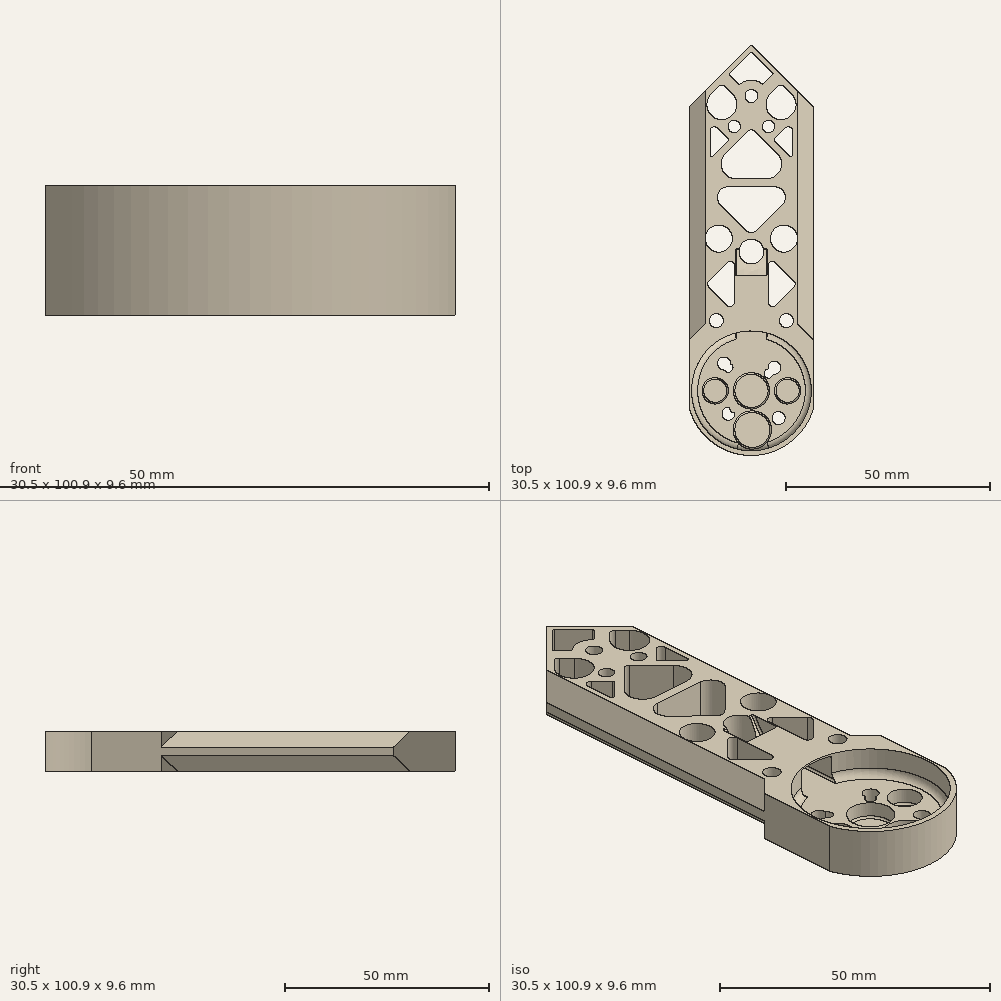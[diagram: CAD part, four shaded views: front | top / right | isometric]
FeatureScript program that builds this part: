
annotation { "Feature Type Name" : "Feature", "Feature Type Description" : "" }
export const myFeature = defineFeature(function(context is Context, id is Id, definition is map)
    precondition{}
    {
        {
            var Q0;
            Q0=qCreatedBy(makeId("Top.planeOp"),FACE);
            var sketch = newSketch(context, id + "F0", { "sketchPlane" : qUnion([Q0])});
            skLineSegment(sketch, "E0", {"start": v(0, 0) * mm, "end": v(-10, 0) * mm});
            skLineSegment(sketch, "E1", {"start": v(-7.84, 7.84) * mm, "end": v(0, 0) * mm});
            skLineSegment(sketch, "E2", {"start": v(-6.78, -6.78) * mm, "end": v(0, 0) * mm});
            skLineSegment(sketch, "E3", {"start": v(0, 0) * mm, "end": v(-5.66, -5.66) * mm});
            skCircle(sketch, "E4", {"center": v(-5.66, -5.66) * mm, "radius": 1.59 * mm});
            skLineSegment(sketch, "E5", {"start": v(0, 0) * mm, "end": v(-6.72, 6.72) * mm});
            skCircle(sketch, "E6", {"center": v(-6.72, 6.72) * mm, "radius": 1.59 * mm});
            skLineSegment(sketch, "E7", {"start": v(0, 0) * mm, "end": v(-5.66, 5.66) * mm});
            skCircle(sketch, "E8", {"center": v(-5.66, 5.66) * mm, "radius": 1.13 * mm});
            skLineSegment(sketch, "E9.MirrorCS", {"start": v(7.84, -7.84) * mm, "end": v(0, 0) * mm});
            skLineSegment(sketch, "E10.MirrorCS", {"start": v(0, 0) * mm, "end": v(5.66, -5.66) * mm});
            skCircle(sketch, "E11.MirrorC", {"center": v(6.72, -6.72) * mm, "radius": 1.59 * mm});
            skCircle(sketch, "E12.MirrorC", {"center": v(5.66, -5.66) * mm, "radius": 1.13 * mm});
            skLineSegment(sketch, "E13.MirrorCS", {"start": v(0, 0) * mm, "end": v(6.72, -6.72) * mm});
            skCircle(sketch, "E14.MirrorC", {"center": v(5.66, 5.66) * mm, "radius": 1.59 * mm});
            skLineSegment(sketch, "E15.MirrorCS", {"start": v(0, 0) * mm, "end": v(5.66, 5.66) * mm});
            skLineSegment(sketch, "E16.MirrorCS", {"start": v(6.78, 6.78) * mm, "end": v(0, 0) * mm});
            skPoint(sketch, "E17.MirrorCS.start.orphan", {"position": v(0, 10) * mm});
            skPoint(sketch, "E18.orphan", {"position": v(10, 10) * mm});
            skPoint(sketch, "E19.orphan", {"position": v(10, -10) * mm});
            skPoint(sketch, "E20.orphan", {"position": v(-10, 10) * mm});
            skPoint(sketch, "E21.orphan", {"position": v(-10, -10) * mm});
            skCircle(sketch, "E22", {"center": v(-4.24, -4.24) * mm, "radius": 1.13 * mm});
            skCircle(sketch, "E23", {"center": v(4.24, 4.24) * mm, "radius": 1.13 * mm});
            skSolve(sketch);
        }
        {
            var Q0;
            Q0=qCreatedBy(makeId("Front.planeOp"),FACE);
            var sketch = newSketch(context, id + "F1", { "sketchPlane" : qUnion([Q0])});
            skLineSegment(sketch, "E24", {"start": v(0, 0) * mm, "end": v(11.35, 0) * mm});
            skLineSegment(sketch, "E25", {"start": v(-11.35, 0) * mm, "end": v(0, 0) * mm});
            skLineSegment(sketch, "E26", {"start": v(0, 0) * mm, "end": v(0, 3.8) * mm});
            skLineSegment(sketch, "E27", {"start": v(0, 3.8) * mm, "end": v(15.25, 3.8) * mm});
            skLineSegment(sketch, "E28", {"start": v(-15.25, 3.8) * mm, "end": v(0, 3.8) * mm});
            skPoint(sketch, "E29.orphan", {"position": v(15.25, 0) * mm});
            skPoint(sketch, "E30.orphan", {"position": v(-15.25, 0) * mm});
            skLineSegment(sketch, "E31", {"start": v(-15.25, 3.8) * mm, "end": v(-11.35, 0) * mm});
            skLineSegment(sketch, "E32", {"start": v(15.25, 3.8) * mm, "end": v(11.35, 0) * mm});
            skLineSegment(sketch, "E33", {"start": v(15.25, 3.8) * mm, "end": v(15.25, 5.8) * mm});
            skLineSegment(sketch, "E34", {"start": v(15.25, 5.8) * mm, "end": v(11.35, 9.6) * mm});
            skLineSegment(sketch, "E35", {"start": v(11.35, 9.6) * mm, "end": v(0, 9.6) * mm});
            skLineSegment(sketch, "E36.MirrorCS", {"start": v(-11.35, 9.6) * mm, "end": v(0, 9.6) * mm});
            skLineSegment(sketch, "E37.MirrorCS", {"start": v(-15.25, 5.8) * mm, "end": v(-11.35, 9.6) * mm});
            skLineSegment(sketch, "E38.MirrorCS", {"start": v(-15.25, 3.8) * mm, "end": v(-15.25, 5.8) * mm});
            skSolve(sketch);
        }
        {
            var Q0;
            Q0=qSketchRegion(id+"F1",true);
            extrude(context, id + "F2", {"entities" : qUnion([Q0]), "depth" : 16.3 * mm, "hasSecondDirection" : true, "secondDirectionOppositeDirection" : true, "secondDirectionDepth" : 85 * mm});
        }
        {
            var Q0;
            Q0=qCreatedBy(makeId("Top.planeOp"),FACE);
            cPlane(context, id + "F3", {"entities" : qUnion([Q0]), "cplaneType" : CPlaneType.OFFSET, "offset" : 16 * mm, "width" : 150 * mm, "height" : 150 * mm});
        }
        {
            var Q0;
            Q0=makeQuery(id+"F2.opExtrude","SWEPT_FACE",FACE,{"disambiguationData":[OSD([sQuery(id+"F1.wireOp",EDGE,"E35"),sQuery(id+"F1.wireOp",EDGE,"E36.MirrorCS")])]});
            var sketch = newSketch(context, id + "F4", { "sketchPlane" : qUnion([Q0])});
            skCircle(sketch, "E39", {"center": v(0, 0) * mm, "radius": 14.75 * mm});
            skLineSegment(sketch, "E40", {"start": v(14.75, 0) * mm, "end": v(-14.75, 0) * mm});
            skSolve(sketch);
        }
        {
            var Q0;
            {var subQ0=sQuery(id+"F4.wireOp",EDGE,"E39");var subQ1=makeQuery(id+"F2.opExtrude","SWEPT_EDGE",EDGE,{"disambiguationData":[OSD([sQuery(id+"F1.wireOp",EDGE,"E34"),sQuery(id+"F1.wireOp",EDGE,"E35")])]});var subQ2=makeQuery(id+"F4.imprint","INTERSECT",VERTEX,{"disambiguationData":[OD(0.0)],"derivedFrom":[subQ1,subQ0]});Q0=makeQuery(id+"F4.imprint","IMPRINT",FACE,{"disambiguationData":[TD([[makeQuery(id+"F4.imprint","IMPRINT",EDGE,{"disambiguationData":[TD([[subQ2,-1.0]])],"derivedFrom":subQ0}),1.0]])]});}
            var Q1;
            {var subQ0=sQuery(id+"F4.wireOp",EDGE,"E39");var subQ1=makeQuery(id+"F2.opExtrude","SWEPT_EDGE",EDGE,{"disambiguationData":[OSD([sQuery(id+"F1.wireOp",EDGE,"E36.MirrorCS"),sQuery(id+"F1.wireOp",EDGE,"E37.MirrorCS")])]});var subQ2=makeQuery(id+"F4.imprint","INTERSECT",VERTEX,{"disambiguationData":[OD(1.0)],"derivedFrom":[subQ1,subQ0]});Q1=makeQuery(id+"F4.imprint","IMPRINT",FACE,{"disambiguationData":[TD([[makeQuery(id+"F4.imprint","IMPRINT",EDGE,{"disambiguationData":[TD([[subQ2,-1.0]])],"derivedFrom":subQ0}),1.0]])]});}
            var Q2;
            {var subQ0=sQuery(id+"F4.wireOp",EDGE,"E40");var subQ1=sQuery(id+"F4.wireOp",EDGE,"E39");var subQ2=makeQuery(id+"F4.imprint","INTERSECT",VERTEX,{"disambiguationData":[OD(1.0)],"derivedFrom":[subQ1,subQ0]});Q2=makeQuery(id+"F4.imprint","IMPRINT",FACE,{"disambiguationData":[TD([[makeQuery(id+"F4.imprint","IMPRINT",EDGE,{"disambiguationData":[TD([[subQ2,-1.0]])],"derivedFrom":subQ1}),1.0]])]});}
            var Q3;
            {var subQ0=sQuery(id+"F4.wireOp",EDGE,"E40");var subQ1=sQuery(id+"F4.wireOp",EDGE,"E39");var subQ2=makeQuery(id+"F4.imprint","INTERSECT",VERTEX,{"disambiguationData":[OD(1.0)],"derivedFrom":[subQ1,subQ0]});Q3=makeQuery(id+"F4.imprint","IMPRINT",FACE,{"disambiguationData":[TD([[makeQuery(id+"F4.imprint","IMPRINT",EDGE,{"disambiguationData":[TD([[subQ2,1.0]])],"derivedFrom":subQ1}),1.0]])]});}
            var Q4;
            {var subQ0=sQuery(id+"F4.wireOp",EDGE,"E40");var subQ1=sQuery(id+"F4.wireOp",EDGE,"E39");var subQ2=makeQuery(id+"F4.imprint","INTERSECT",VERTEX,{"disambiguationData":[OD(0.0)],"derivedFrom":[subQ1,subQ0]});Q4=makeQuery(id+"F4.imprint","IMPRINT",FACE,{"disambiguationData":[TD([[makeQuery(id+"F4.imprint","IMPRINT",EDGE,{"disambiguationData":[TD([[subQ2,-1.0]])],"derivedFrom":subQ1}),1.0]])]});}
            var Q5;
            {var subQ0=sQuery(id+"F4.wireOp",EDGE,"E40");var subQ1=sQuery(id+"F4.wireOp",EDGE,"E39");var subQ2=makeQuery(id+"F4.imprint","INTERSECT",VERTEX,{"disambiguationData":[OD(0.0)],"derivedFrom":[subQ1,subQ0]});Q5=makeQuery(id+"F4.imprint","IMPRINT",FACE,{"disambiguationData":[TD([[makeQuery(id+"F4.imprint","IMPRINT",EDGE,{"disambiguationData":[TD([[subQ2,1.0]])],"derivedFrom":subQ1}),1.0]])]});}
            extrude(context, id + "F5", {"entities" : qUnion([Q0, Q1, Q2, Q3, Q4, Q5]), "operationType" : NewBodyOperationType.REMOVE, "oppositeDirection" : true, "depth" : 5.6 * mm});
        }
        {
            var Q0;
            {var subQ5=sQuery(id+"F0.wireOp",EDGE,"E1");Q0=makeQuery(id+"F0.imprint","IMPRINT",FACE,{"disambiguationData":[TD([[makeQuery(id+"F0.imprint","IMPRINT",EDGE,{"derivedFrom":subQ5}),-1.0]])]});}
            var Q1;
            {var subQ3=sQuery(id+"F0.wireOp",EDGE,"E1");Q1=makeQuery(id+"F0.imprint","IMPRINT",FACE,{"disambiguationData":[TD([[makeQuery(id+"F0.imprint","IMPRINT",EDGE,{"derivedFrom":subQ3}),1.0]])]});}
            var Q2;
            {var subQ5=sQuery(id+"F0.wireOp",EDGE,"E2");Q2=makeQuery(id+"F0.imprint","IMPRINT",FACE,{"disambiguationData":[TD([[makeQuery(id+"F0.imprint","IMPRINT",EDGE,{"derivedFrom":subQ5}),1.0]])]});}
            var Q3;
            {var subQ5=sQuery(id+"F0.wireOp",EDGE,"E2");Q3=makeQuery(id+"F0.imprint","IMPRINT",FACE,{"disambiguationData":[TD([[makeQuery(id+"F0.imprint","IMPRINT",EDGE,{"derivedFrom":subQ5}),-1.0]])]});}
            var Q4;
            {var subQ0=sQuery(id+"F0.wireOp",EDGE,"E22");var subQ3=sQuery(id+"F0.wireOp",EDGE,"E3");var subQ4=makeQuery(id+"F0.imprint","INTERSECT",VERTEX,{"disambiguationData":[OD(0.0)],"derivedFrom":[subQ3,subQ0]});Q4=makeQuery(id+"F0.imprint","IMPRINT",FACE,{"disambiguationData":[TD([[makeQuery(id+"F0.imprint","IMPRINT",EDGE,{"disambiguationData":[TD([[subQ4,-1.0]])],"derivedFrom":subQ3}),1.0]])]});}
            var Q5;
            {var subQ0=sQuery(id+"F0.wireOp",EDGE,"E22");var subQ3=sQuery(id+"F0.wireOp",EDGE,"E3");var subQ4=makeQuery(id+"F0.imprint","INTERSECT",VERTEX,{"disambiguationData":[OD(0.0)],"derivedFrom":[subQ3,subQ0]});Q5=makeQuery(id+"F0.imprint","IMPRINT",FACE,{"disambiguationData":[TD([[makeQuery(id+"F0.imprint","IMPRINT",EDGE,{"disambiguationData":[TD([[subQ4,-1.0]])],"derivedFrom":subQ3}),-1.0]])]});}
            var Q6;
            {var subQ1=sQuery(id+"F0.wireOp",EDGE,"E6");var subQ3=sQuery(id+"F0.wireOp",EDGE,"E8");var subQ5=makeQuery(id+"F0.imprint","INTERSECT",VERTEX,{"disambiguationData":[OD(0.0)],"derivedFrom":[subQ1,subQ3]});Q6=makeQuery(id+"F0.imprint","IMPRINT",FACE,{"disambiguationData":[TD([[makeQuery(id+"F0.imprint","IMPRINT",EDGE,{"disambiguationData":[TD([[subQ5,-1.0]])],"derivedFrom":subQ1}),-1.0]])]});}
            var Q7;
            {var subQ1=sQuery(id+"F0.wireOp",EDGE,"E6");var subQ3=sQuery(id+"F0.wireOp",EDGE,"E8");var subQ5=makeQuery(id+"F0.imprint","INTERSECT",VERTEX,{"disambiguationData":[OD(1.0)],"derivedFrom":[subQ1,subQ3]});Q7=makeQuery(id+"F0.imprint","IMPRINT",FACE,{"disambiguationData":[TD([[makeQuery(id+"F0.imprint","IMPRINT",EDGE,{"disambiguationData":[TD([[subQ5,1.0]])],"derivedFrom":subQ1}),-1.0]])]});}
            var Q8;
            {var subQ3=sQuery(id+"F0.wireOp",EDGE,"E9.MirrorCS");Q8=makeQuery(id+"F0.imprint","IMPRINT",FACE,{"disambiguationData":[TD([[makeQuery(id+"F0.imprint","IMPRINT",EDGE,{"derivedFrom":subQ3}),1.0]])]});}
            var Q9;
            {var subQ3=sQuery(id+"F0.wireOp",EDGE,"E9.MirrorCS");Q9=makeQuery(id+"F0.imprint","IMPRINT",FACE,{"disambiguationData":[TD([[makeQuery(id+"F0.imprint","IMPRINT",EDGE,{"derivedFrom":subQ3}),-1.0]])]});}
            var Q10;
            {var subQ1=sQuery(id+"F0.wireOp",EDGE,"E11.MirrorC");var subQ3=sQuery(id+"F0.wireOp",EDGE,"E12.MirrorC");var subQ5=makeQuery(id+"F0.imprint","INTERSECT",VERTEX,{"disambiguationData":[OD(0.0)],"derivedFrom":[subQ1,subQ3]});Q10=makeQuery(id+"F0.imprint","IMPRINT",FACE,{"disambiguationData":[TD([[makeQuery(id+"F0.imprint","IMPRINT",EDGE,{"disambiguationData":[TD([[subQ5,-1.0]])],"derivedFrom":subQ1}),1.0]])]});}
            var Q11;
            {var subQ1=sQuery(id+"F0.wireOp",EDGE,"E11.MirrorC");var subQ3=sQuery(id+"F0.wireOp",EDGE,"E12.MirrorC");var subQ5=makeQuery(id+"F0.imprint","INTERSECT",VERTEX,{"disambiguationData":[OD(1.0)],"derivedFrom":[subQ1,subQ3]});Q11=makeQuery(id+"F0.imprint","IMPRINT",FACE,{"disambiguationData":[TD([[makeQuery(id+"F0.imprint","IMPRINT",EDGE,{"disambiguationData":[TD([[subQ5,1.0]])],"derivedFrom":subQ1}),1.0]])]});}
            var Q12;
            {var subQ0=sQuery(id+"F0.wireOp",EDGE,"E23");var subQ1=sQuery(id+"F0.wireOp",EDGE,"E14.MirrorC");var subQ2=makeQuery(id+"F0.imprint","INTERSECT",VERTEX,{"disambiguationData":[OD(1.0)],"derivedFrom":[subQ1,subQ0]});Q12=makeQuery(id+"F0.imprint","IMPRINT",FACE,{"disambiguationData":[TD([[makeQuery(id+"F0.imprint","IMPRINT",EDGE,{"disambiguationData":[TD([[subQ2,1.0]])],"derivedFrom":subQ1}),1.0]])]});}
            var Q13;
            {var subQ1=sQuery(id+"F0.wireOp",EDGE,"E16.MirrorCS");var subQ5=makeQuery(id+"F0.imprint","IMPRINT",VERTEX,{"derivedFrom":subQ1});Q13=makeQuery(id+"F0.imprint","IMPRINT",FACE,{"disambiguationData":[TD([[makeQuery(id+"F0.imprint","IMPRINT",EDGE,{"disambiguationData":[TD([[subQ5,1.0]])],"derivedFrom":subQ1}),-1.0]])]});}
            var Q14;
            {var subQ1=sQuery(id+"F0.wireOp",EDGE,"E16.MirrorCS");var subQ5=makeQuery(id+"F0.imprint","IMPRINT",VERTEX,{"derivedFrom":subQ1});Q14=makeQuery(id+"F0.imprint","IMPRINT",FACE,{"disambiguationData":[TD([[makeQuery(id+"F0.imprint","IMPRINT",EDGE,{"disambiguationData":[TD([[subQ5,1.0]])],"derivedFrom":subQ1}),1.0]])]});}
            var Q15;
            {var subQ1=sQuery(id+"F0.wireOp",EDGE,"E3");var subQ3=sQuery(id+"F0.wireOp",EDGE,"E4");var subQ5=makeQuery(id+"F0.imprint","INTERSECT",VERTEX,{"derivedFrom":[subQ1,subQ3]});Q15=makeQuery(id+"F0.imprint","IMPRINT",FACE,{"disambiguationData":[TD([[makeQuery(id+"F0.imprint","IMPRINT",EDGE,{"disambiguationData":[TD([[subQ5,-1.0]])],"derivedFrom":subQ1}),1.0]])]});}
            var Q16;
            {var subQ1=sQuery(id+"F0.wireOp",EDGE,"E3");var subQ3=sQuery(id+"F0.wireOp",EDGE,"E4");var subQ5=makeQuery(id+"F0.imprint","INTERSECT",VERTEX,{"derivedFrom":[subQ1,subQ3]});Q16=makeQuery(id+"F0.imprint","IMPRINT",FACE,{"disambiguationData":[TD([[makeQuery(id+"F0.imprint","IMPRINT",EDGE,{"disambiguationData":[TD([[subQ5,-1.0]])],"derivedFrom":subQ1}),-1.0]])]});}
            var Q17;
            {var subQ0=sQuery(id+"F0.wireOp",EDGE,"E13.MirrorCS");var subQ3=makeQuery(id+"F0.imprint","IMPRINT",VERTEX,{"derivedFrom":subQ0});Q17=makeQuery(id+"F0.imprint","IMPRINT",FACE,{"disambiguationData":[TD([[makeQuery(id+"F0.imprint","IMPRINT",EDGE,{"disambiguationData":[TD([[subQ3,1.0]])],"derivedFrom":subQ0}),1.0]])]});}
            var Q18;
            {var subQ0=sQuery(id+"F0.wireOp",EDGE,"E23");var subQ3=sQuery(id+"F0.wireOp",EDGE,"E14.MirrorC");var subQ4=makeQuery(id+"F0.imprint","INTERSECT",VERTEX,{"disambiguationData":[OD(1.0)],"derivedFrom":[subQ3,subQ0]});Q18=makeQuery(id+"F0.imprint","IMPRINT",FACE,{"disambiguationData":[TD([[makeQuery(id+"F0.imprint","IMPRINT",EDGE,{"disambiguationData":[TD([[subQ4,1.0]])],"derivedFrom":subQ3}),-1.0]])]});}
            var Q19;
            {var subQ0=sQuery(id+"F0.wireOp",EDGE,"E23");var subQ1=sQuery(id+"F0.wireOp",EDGE,"E14.MirrorC");var subQ2=makeQuery(id+"F0.imprint","INTERSECT",VERTEX,{"disambiguationData":[OD(0.0)],"derivedFrom":[subQ1,subQ0]});Q19=makeQuery(id+"F0.imprint","IMPRINT",FACE,{"disambiguationData":[TD([[makeQuery(id+"F0.imprint","IMPRINT",EDGE,{"disambiguationData":[TD([[subQ2,-1.0]])],"derivedFrom":subQ1}),1.0]])]});}
            var Q20;
            {var subQ0=sQuery(id+"F0.wireOp",EDGE,"E23");var subQ3=sQuery(id+"F0.wireOp",EDGE,"E14.MirrorC");var subQ4=makeQuery(id+"F0.imprint","INTERSECT",VERTEX,{"disambiguationData":[OD(0.0)],"derivedFrom":[subQ3,subQ0]});Q20=makeQuery(id+"F0.imprint","IMPRINT",FACE,{"disambiguationData":[TD([[makeQuery(id+"F0.imprint","IMPRINT",EDGE,{"disambiguationData":[TD([[subQ4,-1.0]])],"derivedFrom":subQ3}),-1.0]])]});}
            var Q21;
            {var subQ0=sQuery(id+"F0.wireOp",EDGE,"E13.MirrorCS");var subQ3=makeQuery(id+"F0.imprint","IMPRINT",VERTEX,{"derivedFrom":subQ0});Q21=makeQuery(id+"F0.imprint","IMPRINT",FACE,{"disambiguationData":[TD([[makeQuery(id+"F0.imprint","IMPRINT",EDGE,{"disambiguationData":[TD([[subQ3,1.0]])],"derivedFrom":subQ0}),-1.0]])]});}
            var Q22;
            {var subQ1=sQuery(id+"F0.wireOp",EDGE,"E5");var subQ5=sQuery(id+"F0.wireOp",EDGE,"E7");var subQ7=makeQuery(id+"F0.imprint","INTERSECT",VERTEX,{"derivedFrom":[subQ1,subQ5]});Q22=makeQuery(id+"F0.imprint","IMPRINT",FACE,{"disambiguationData":[TD([[makeQuery(id+"F0.imprint","IMPRINT",EDGE,{"disambiguationData":[TD([[subQ7,-1.0]])],"derivedFrom":subQ1}),1.0]])]});}
            var Q23;
            {var subQ1=sQuery(id+"F0.wireOp",EDGE,"E5");var subQ5=sQuery(id+"F0.wireOp",EDGE,"E7");var subQ7=makeQuery(id+"F0.imprint","INTERSECT",VERTEX,{"derivedFrom":[subQ1,subQ5]});Q23=makeQuery(id+"F0.imprint","IMPRINT",FACE,{"disambiguationData":[TD([[makeQuery(id+"F0.imprint","IMPRINT",EDGE,{"disambiguationData":[TD([[subQ7,-1.0]])],"derivedFrom":subQ1}),-1.0]])]});}
            extrude(context, id + "F6", {"entities" : qUnion([Q0, Q1, Q2, Q3, Q4, Q5, Q6, Q7, Q8, Q9, Q10, Q11, Q12, Q13, Q14, Q15, Q16, Q17, Q18, Q19, Q20, Q21, Q22, Q23]), "operationType" : NewBodyOperationType.REMOVE, "endBound" : BoundingType.THROUGH_ALL, "depth" : 5 * mm});
        }
        {
            var Q0;
            Q0=qCreatedBy(makeId("Top.planeOp"),FACE);
            var sketch = newSketch(context, id + "F7", { "sketchPlane" : qUnion([Q0])});
            skCircle(sketch, "E41", {"center": v(0, 0) * mm, "radius": 14.75 * mm});
            skArc(sketch, "E42", {"start": v(15.25, 4.5) * mm, "mid": v(0, 15.9) * mm, "end": v(-15.25, 4.5) * mm});
            skLineSegment(sketch, "E43", {"start": v(0, 0) * mm, "end": v(15.25, 0) * mm});
            skLineSegment(sketch, "E44", {"start": v(15.25, 0) * mm, "end": v(15.25, 4.5) * mm});
            skLineSegment(sketch, "E45.MirrorCS", {"start": v(15.25, 0) * mm, "end": v(15.25, -4.5) * mm});
            skLineSegment(sketch, "E46.MirrorCS", {"start": v(-15.25, 0) * mm, "end": v(-15.25, 4.5) * mm});
            skLineSegment(sketch, "E47.MirrorCS", {"start": v(-15.25, 0) * mm, "end": v(-15.25, -4.5) * mm});
            skArc(sketch, "E48.trimOffspring", {"start": v(-15.25, -4.5) * mm, "mid": v(0, -15.9) * mm, "end": v(15.25, -4.5) * mm});
            skSolve(sketch);
        }
        {
            var Q0;
            Q0=qSketchRegion(id+"F7",true);
            var Q1;
            Q1=makeQuery(id+"F2.opExtrude","SWEPT_FACE",FACE,{"disambiguationData":[OSD([sQuery(id+"F1.wireOp",EDGE,"E35"),sQuery(id+"F1.wireOp",EDGE,"E36.MirrorCS")])]});
            extrude(context, id + "F8", {"entities" : qUnion([Q0]), "operationType" : NewBodyOperationType.ADD, "endBound" : BoundingType.UP_TO_SURFACE, "endBoundEntityFace" : qUnion([Q1]), "depth" : 15.75 * mm});
        }
        {
            var Q0;
            Q0=qCreatedBy(id+"F3.planeOp",FACE);
            var sketch = newSketch(context, id + "F9", { "sketchPlane" : qUnion([Q0])});
            skCircle(sketch, "E49", {"center": v(0, 0) * mm, "radius": 15.9 * mm});
            skLineSegment(sketch, "E50", {"start": v(-15.9, 0) * mm, "end": v(-15.9, -16.3) * mm});
            skLineSegment(sketch, "E51.bottom", {"start": v(-15.9, -16.3) * mm, "end": v(15.9, -16.3) * mm});
            skLineSegment(sketch, "E51.top", {"start": v(-15.9, 0) * mm, "end": v(15.9, 0) * mm});
            skLineSegment(sketch, "E51.left", {"start": v(-15.9, -16.3) * mm, "end": v(-15.9, 0) * mm});
            skLineSegment(sketch, "E51.right", {"start": v(15.9, -16.3) * mm, "end": v(15.9, 0) * mm});
            skLineSegment(sketch, "E52", {"start": v(0, 0) * mm, "end": v(-3.75, 0) * mm});
            skLineSegment(sketch, "E53.bottom", {"start": v(-3.75, -16.3) * mm, "end": v(3.75, -16.3) * mm});
            skSolve(sketch);
        }
        {
            var Q0;
            {var subQ3=sQuery(id+"F9.wireOp",EDGE,"E51.left");Q0=makeQuery(id+"F9.imprint","IMPRINT",FACE,{"disambiguationData":[TD([[makeQuery(id+"F9.imprint","IMPRINT",EDGE,{"derivedFrom":subQ3}),-1.0]])]});}
            var Q1;
            {var subQ3=sQuery(id+"F9.wireOp",EDGE,"E51.left");Q1=makeQuery(id+"F9.imprint","IMPRINT",FACE,{"disambiguationData":[TD([[makeQuery(id+"F9.imprint","IMPRINT",EDGE,{"derivedFrom":subQ3}),-1.0]])]});}
            var Q2;
            {var subQ0=sQuery(id+"F9.wireOp",EDGE,"E51.right");Q2=makeQuery(id+"F9.imprint","IMPRINT",FACE,{"disambiguationData":[TD([[makeQuery(id+"F9.imprint","IMPRINT",EDGE,{"derivedFrom":subQ0}),1.0]])]});}
            extrude(context, id + "F10", {"entities" : qUnion([Q0, Q1, Q2]), "operationType" : NewBodyOperationType.REMOVE, "oppositeDirection" : true, "depth" : 25 * mm});
        }
        {
            var Q0;
            Q0=makeQuery(id+"F5.boolean.opBoolean","COPY",FACE,{"derivedFrom":makeQuery(id+"F5.opExtrude","CAP_FACE",FACE,{"disambiguationData":[OSD([sQuery(id+"F4.wireOp",EDGE,"E39")])],"isStart":false})});
            var sketch = newSketch(context, id + "F11", { "sketchPlane" : qUnion([Q0])});
            skCircle(sketch, "E54", {"center": v(0, 0) * mm, "radius": 4.47 * mm});
            skLineSegment(sketch, "E55", {"start": v(0, 0) * mm, "end": v(8.91, 0) * mm});
            skCircle(sketch, "E56", {"center": v(0.24, -9.63) * mm, "radius": 4.72 * mm});
            skLineSegment(sketch, "E57.MirrorCS", {"start": v(0, 0) * mm, "end": v(-8.91, 0) * mm});
            skCircle(sketch, "E58", {"center": v(8.91, 0) * mm, "radius": 3.24 * mm});
            skCircle(sketch, "E59.MirrorC", {"center": v(-8.91, 0) * mm, "radius": 3.24 * mm});
            skSolve(sketch);
        }
        {
            var Q0;
            Q0=qSketchRegion(id+"F11",true);
            extrude(context, id + "F12", {"entities" : qUnion([Q0]), "operationType" : NewBodyOperationType.REMOVE, "oppositeDirection" : true, "depth" : 3.2 * mm});
        }
        {
            var Q0;
            Q0=qCreatedBy(makeId("Top.planeOp"),FACE);
            cPlane(context, id + "F13", {"entities" : qUnion([Q0]), "cplaneType" : CPlaneType.OFFSET, "offset" : 0 * mm, "width" : 150 * mm, "height" : 150 * mm});
        }
        {
            var Q0;
            Q0=qCreatedBy(makeId("Top.planeOp"),FACE);
            var sketch = newSketch(context, id + "F14", { "sketchPlane" : qUnion([Q0])});
            skLineSegment(sketch, "E60", {"start": v(0, 69.75) * mm, "end": v(15.25, 69.75) * mm});
            skLineSegment(sketch, "E61", {"start": v(15.25, 69.75) * mm, "end": v(0, 85) * mm});
            skLineSegment(sketch, "E62.MirrorCS", {"start": v(-15.25, 69.75) * mm, "end": v(0, 85) * mm});
            skLineSegment(sketch, "E63.MirrorCS", {"start": v(0, 69.75) * mm, "end": v(-15.25, 69.75) * mm});
            skLineSegment(sketch, "E64", {"start": v(-15.25, 69.75) * mm, "end": v(-15.25, 85) * mm});
            skLineSegment(sketch, "E65", {"start": v(-15.25, 85) * mm, "end": v(15.25, 85) * mm});
            skLineSegment(sketch, "E66", {"start": v(15.25, 85) * mm, "end": v(15.25, 69.75) * mm});
            skSolve(sketch);
        }
        {
            var Q0;
            Q0=makeQuery(id+"F14.imprint","IMPRINT",FACE,{"disambiguationData":[TD([[makeQuery(id+"F14.imprint","IMPRINT",EDGE,{"derivedFrom":sQuery(id+"F14.wireOp",EDGE,"E61")}),-1.0]])]});
            var Q1;
            {var subQ0=sQuery(id+"F14.wireOp",EDGE,"E62.MirrorCS");Q1=makeQuery(id+"F14.imprint","IMPRINT",FACE,{"disambiguationData":[TD([[makeQuery(id+"F14.imprint","IMPRINT",EDGE,{"derivedFrom":subQ0}),1.0]])]});}
            extrude(context, id + "F15", {"entities" : qUnion([Q0, Q1]), "operationType" : NewBodyOperationType.REMOVE, "depth" : 25 * mm});
        }
        {
            var Q0;
            {var subQ0=sQuery(id+"F1.wireOp",EDGE,"E38.MirrorCS");var subQ1=sQuery(id+"F1.wireOp",EDGE,"E37.MirrorCS");var subQ2=sQuery(id+"F1.wireOp",EDGE,"E36.MirrorCS");var subQ3=sQuery(id+"F1.wireOp",EDGE,"E35");var subQ4=sQuery(id+"F1.wireOp",EDGE,"E34");var subQ5=sQuery(id+"F1.wireOp",EDGE,"E33");var subQ6=sQuery(id+"F1.wireOp",EDGE,"E32");var subQ7=sQuery(id+"F1.wireOp",EDGE,"E31");var subQ8=sQuery(id+"F1.wireOp",EDGE,"E25");var subQ9=sQuery(id+"F1.wireOp",EDGE,"E24");var subQ13=makeQuery(id+"F2.opExtrude","SWEPT_FACE",FACE,{"disambiguationData":[OSD([subQ3,subQ2])]});Q0=makeQuery(id+"F8.boolean.opBoolean","MERGE",FACE,{"derivedFrom":[makeQuery(id+"F5.boolean.opBoolean","SPLIT",FACE,{"disambiguationData":[TD([makeQuery(id+"F2.opExtrude","CAP_FACE",FACE,{"disambiguationData":[OSD([subQ9,subQ8,subQ7,subQ6,subQ5,subQ4,subQ3,subQ2,subQ1,subQ0])],"isStart":true})])],"derivedFrom":subQ13}),makeQuery(id+"F5.boolean.opBoolean","SPLIT",FACE,{"disambiguationData":[TD([makeQuery(id+"F2.opExtrude","CAP_FACE",FACE,{"disambiguationData":[OSD([subQ9,subQ8,subQ7,subQ6,subQ5,subQ4,subQ3,subQ2,subQ1,subQ0])],"isStart":false})])],"derivedFrom":subQ13}),makeQuery(id+"F8.opExtrude","CAP_FACE",FACE,{"disambiguationData":[OSD([sQuery(id+"F7.wireOp",EDGE,"E41"),sQuery(id+"F7.wireOp",EDGE,"E42")])],"isStart":false})]});}
            var sketch = newSketch(context, id + "F16", { "sketchPlane" : qUnion([Q0])});
            skLineSegment(sketch, "E67", {"start": v(0, 85) * mm, "end": v(0, 72.5) * mm});
            skCircle(sketch, "E68", {"center": v(0, 72.5) * mm, "radius": 1.6 * mm});
            skLineSegment(sketch, "E69.0", {"start": v(5.2, 78.2) * mm, "end": v(0.28, 83.12) * mm});
            skLineSegment(sketch, "E69.1", {"start": v(-5.23, 78.17) * mm, "end": v(-0.28, 83.12) * mm});
            skPoint(sketch, "E70.visualSharp", {"position": v(0, 83.4) * mm});
            skArc(sketch, "E70.filletArc", {"start": v(0.28, 83.12) * mm, "mid": v(0, 83.23) * mm, "end": v(-0.28, 83.12) * mm});
            skArc(sketch, "E71", {"start": v(2.58, 75.55) * mm, "mid": v(-0.02, 76.5) * mm, "end": v(-2.62, 75.52) * mm});
            skLineSegment(sketch, "E72.trimOffspring", {"start": v(-3.16, 75.54) * mm, "end": v(-5.23, 77.6) * mm});
            skLineSegment(sketch, "E73.trimOffspring", {"start": v(3.12, 75.58) * mm, "end": v(5.2, 77.64) * mm});
            skPoint(sketch, "E74.visualSharp", {"position": v(-5.51, 77.89) * mm});
            skArc(sketch, "E74.filletArc", {"start": v(-5.23, 78.17) * mm, "mid": v(-5.35, 77.89) * mm, "end": v(-5.23, 77.6) * mm});
            skPoint(sketch, "E75.visualSharp", {"position": v(5.47, 77.93) * mm});
            skArc(sketch, "E75.filletArc", {"start": v(5.2, 77.64) * mm, "mid": v(5.3, 77.93) * mm, "end": v(5.2, 78.2) * mm});
            skPoint(sketch, "E76.visualSharp", {"position": v(-2.89, 75.27) * mm});
            skArc(sketch, "E76.filletArc", {"start": v(-3.16, 75.54) * mm, "mid": v(-2.9, 75.43) * mm, "end": v(-2.62, 75.52) * mm});
            skPoint(sketch, "E77.visualSharp", {"position": v(2.85, 75.3) * mm});
            skArc(sketch, "E77.filletArc", {"start": v(2.58, 75.55) * mm, "mid": v(2.86, 75.46) * mm, "end": v(3.12, 75.58) * mm});
            skSolve(sketch);
        }
        {
            var Q0;
            {var subQ4=sQuery(id+"F16.wireOp",EDGE,"E69.0");Q0=makeQuery(id+"F16.imprint","IMPRINT",FACE,{"disambiguationData":[TD([[makeQuery(id+"F16.imprint","IMPRINT",EDGE,{"derivedFrom":subQ4}),1.0]])]});}
            var Q1;
            {var subQ4=sQuery(id+"F16.wireOp",EDGE,"E69.1");Q1=makeQuery(id+"F16.imprint","IMPRINT",FACE,{"disambiguationData":[TD([[makeQuery(id+"F16.imprint","IMPRINT",EDGE,{"derivedFrom":subQ4}),-1.0]])]});}
            var Q2;
            Q2=makeQuery(id+"F16.imprint","IMPRINT",FACE,{"disambiguationData":[TD([[makeQuery(id+"F16.imprint","IMPRINT",EDGE,{"derivedFrom":sQuery(id+"F16.wireOp",EDGE,"E68")}),1.0]])]});
            extrude(context, id + "F17", {"entities" : qUnion([Q0, Q1, Q2]), "operationType" : NewBodyOperationType.REMOVE, "oppositeDirection" : true, "depth" : 25 * mm});
        }
        {
            var Q0;
            Q0=qCreatedBy(makeId("Front.planeOp"),FACE);
            cPlane(context, id + "F18", {"entities" : qUnion([Q0]), "cplaneType" : CPlaneType.OFFSET, "offset" : 14 * mm, "oppositeDirection" : true, "width" : 150 * mm, "height" : 150 * mm});
        }
        {
            var Q0;
            Q0=qCreatedBy(id+"F18.planeOp",FACE);
            var sketch = newSketch(context, id + "F19", { "sketchPlane" : qUnion([Q0])});
            skLineSegment(sketch, "E78", {"start": v(4, 4) * mm, "end": v(4, 9.2) * mm});
            skLineSegment(sketch, "E79.bottom", {"start": v(3.6, 9.2) * mm, "end": v(-3.6, 9.2) * mm});
            skLineSegment(sketch, "E79.left", {"start": v(4, 8.8) * mm, "end": v(4, 4.4) * mm});
            skLineSegment(sketch, "E79.right", {"start": v(-4, 8.8) * mm, "end": v(-4, 4.4) * mm});
            skLineSegment(sketch, "E80", {"start": v(0, 0) * mm, "end": v(0, 4) * mm});
            skLineSegment(sketch, "E81", {"start": v(0, 4) * mm, "end": v(3.6, 4) * mm});
            skLineSegment(sketch, "E82", {"start": v(0, 4) * mm, "end": v(-3.6, 4) * mm});
            skPoint(sketch, "E83.orphan", {"position": v(-4, 0) * mm});
            skPoint(sketch, "E79.top.start.orphan", {"position": v(4, 0) * mm});
            skPoint(sketch, "E84.visualSharp", {"position": v(4, 4) * mm});
            skArc(sketch, "E84.filletArc", {"start": v(3.6, 4) * mm, "mid": v(3.88, 4.12) * mm, "end": v(4, 4.4) * mm});
            skPoint(sketch, "E85.visualSharp", {"position": v(-4, 4) * mm});
            skArc(sketch, "E85.filletArc", {"start": v(-4, 4.4) * mm, "mid": v(-3.88, 4.12) * mm, "end": v(-3.6, 4) * mm});
            skPoint(sketch, "E86.visualSharp", {"position": v(-4, 9.2) * mm});
            skArc(sketch, "E86.filletArc", {"start": v(-3.6, 9.2) * mm, "mid": v(-3.88, 9.08) * mm, "end": v(-4, 8.8) * mm});
            skPoint(sketch, "E87.visualSharp", {"position": v(4, 9.2) * mm});
            skArc(sketch, "E87.filletArc", {"start": v(4, 8.8) * mm, "mid": v(3.88, 9.08) * mm, "end": v(3.6, 9.2) * mm});
            skSolve(sketch);
        }
        {
            var Q0;
            Q0=qCreatedBy(makeId("Right.planeOp"),FACE);
            var sketch = newSketch(context, id + "F20", { "sketchPlane" : qUnion([Q0])});
            skLineSegment(sketch, "E88", {"start": v(0, 0) * mm, "end": v(14.4, 0) * mm});
            skLineSegment(sketch, "E89", {"start": v(14.4, 0) * mm, "end": v(14.4, 4) * mm});
            skLineSegment(sketch, "E90", {"start": v(14.4, 4) * mm, "end": v(26.4, 4) * mm});
            skLineSegment(sketch, "E91", {"start": v(26.4, 4) * mm, "end": v(35, 4) * mm});
            skLineSegment(sketch, "E92", {"start": v(35, 4) * mm, "end": v(35, 9.6) * mm});
            skFitSpline(sketch, "E93", {"points": [v(26.4, 4) * mm, v(30.4, 4.73) * mm, v(32.04, 5.93) * mm, v(33.82, 8.02) * mm, v(35, 9.6) * mm], "startDerivative": vector(21.55, 0) * mm, "endDerivative": vector(8.23, 6.38) * mm});
            skLineSegment(sketch, "E94", {"start": v(35, 9.6) * mm, "end": v(36.63, 9.93) * mm});
            skSolve(sketch);
        }
        {
            var Q0;
            Q0=makeQuery(id+"F19.imprint","IMPRINT",FACE,{"disambiguationData":[TD([[makeQuery(id+"F19.imprint","IMPRINT",EDGE,{"derivedFrom":sQuery(id+"F19.wireOp",EDGE,"E79.bottom")}),1.0]])]});
            var Q1;
            Q1=sQuery(id+"F20.wireOp",EDGE,"E93");
            var Q2;
            Q2=sQuery(id+"F20.wireOp",EDGE,"E90");
            var Q3;
            Q3=sQuery(id+"F20.wireOp",EDGE,"E94");
            sweep(context, id + "F21", {"operationType" : NewBodyOperationType.REMOVE, "profiles" : qUnion([Q0]), "path" : qUnion([Q1, Q2, Q3])});
        }
        {
            var Q0;
            Q0=qCreatedBy(id+"F13.planeOp",FACE);
            var sketch = newSketch(context, id + "F22", { "sketchPlane" : qUnion([Q0])});
            skLineSegment(sketch, "E95", {"start": v(0, 0) * mm, "end": v(0, 37.45) * mm});
            skLineSegment(sketch, "E96", {"start": v(-11.35, 37.45) * mm, "end": v(0, 37.45) * mm});
            skPoint(sketch, "E97.visualSharp", {"position": v(-11.35, 45.75) * mm});
            skLineSegment(sketch, "E98.MirrorCS", {"start": v(11.35, 37.45) * mm, "end": v(0, 37.45) * mm});
            skPoint(sketch, "E99.MirrorP", {"position": v(11.35, 45.75) * mm});
            skLineSegment(sketch, "E100", {"start": v(1.18, 39.4) * mm, "end": v(7.52, 45.52) * mm});
            skLineSegment(sketch, "E101", {"start": v(5.6, 50.25) * mm, "end": v(0, 50.25) * mm});
            skLineSegment(sketch, "E102", {"start": v(0, 50.25) * mm, "end": v(0, 52.25) * mm});
            skLineSegment(sketch, "E103", {"start": v(0, 52.25) * mm, "end": v(3.95, 52.25) * mm});
            skLineSegment(sketch, "E104", {"start": v(6.43, 58.22) * mm, "end": v(0.7, 63.94) * mm});
            skPoint(sketch, "E105.visualSharp", {"position": v(12.4, 52.25) * mm});
            skArc(sketch, "E105.filletArc", {"start": v(3.95, 52.25) * mm, "mid": v(7.18, 54.41) * mm, "end": v(6.43, 58.22) * mm});
            skPoint(sketch, "E106.visualSharp", {"position": v(12.4, 50.25) * mm});
            skArc(sketch, "E106.filletArc", {"start": v(7.52, 45.52) * mm, "mid": v(8.15, 48.53) * mm, "end": v(5.6, 50.25) * mm});
            skLineSegment(sketch, "E107.MirrorCS", {"start": v(-6.43, 58.22) * mm, "end": v(-0.7, 63.94) * mm});
            skLineSegment(sketch, "E108.MirrorCS", {"start": v(-5.6, 50.25) * mm, "end": v(0, 50.25) * mm});
            skLineSegment(sketch, "E109.MirrorCS", {"start": v(0, 52.25) * mm, "end": v(-3.95, 52.25) * mm});
            skArc(sketch, "E110.MirrorCS", {"start": v(-3.95, 52.25) * mm, "mid": v(-7.18, 54.41) * mm, "end": v(-6.43, 58.22) * mm});
            skArc(sketch, "E111.MirrorCS", {"start": v(-7.52, 45.52) * mm, "mid": v(-8.15, 48.53) * mm, "end": v(-5.6, 50.25) * mm});
            skLineSegment(sketch, "E112.MirrorCS", {"start": v(-1.18, 39.4) * mm, "end": v(-7.52, 45.52) * mm});
            skPoint(sketch, "E113.visualSharp", {"position": v(0, 64.65) * mm});
            skArc(sketch, "E113.filletArc", {"start": v(0.7, 63.94) * mm, "mid": v(0, 64.24) * mm, "end": v(-0.7, 63.94) * mm});
            skPoint(sketch, "E114.visualSharp", {"position": v(0, 38.25) * mm});
            skArc(sketch, "E114.filletArc", {"start": v(-1.18, 39.4) * mm, "mid": v(0, 38.92) * mm, "end": v(1.18, 39.4) * mm});
            skLineSegment(sketch, "E115", {"start": v(-11.2, 26.25) * mm, "end": v(-4.2, 26.25) * mm});
            skLineSegment(sketch, "E116", {"start": v(-4.2, 26.25) * mm, "end": v(-4.2, 30.84) * mm});
            skLineSegment(sketch, "E117", {"start": v(-5.9, 31.54) * mm, "end": v(-10.5, 26.96) * mm});
            skLineSegment(sketch, "E118.MirrorCS", {"start": v(-4.2, 26.25) * mm, "end": v(-4.2, 21.66) * mm});
            skLineSegment(sketch, "E119.MirrorCS", {"start": v(-5.9, 20.96) * mm, "end": v(-10.5, 25.54) * mm});
            skPoint(sketch, "E120.visualSharp", {"position": v(-4.2, 33.25) * mm});
            skArc(sketch, "E120.filletArc", {"start": v(-4.2, 30.84) * mm, "mid": v(-4.82, 31.76) * mm, "end": v(-5.9, 31.54) * mm});
            skPoint(sketch, "E121.visualSharp", {"position": v(-4.2, 19.25) * mm});
            skArc(sketch, "E121.filletArc", {"start": v(-5.9, 20.96) * mm, "mid": v(-4.82, 20.74) * mm, "end": v(-4.2, 21.66) * mm});
            skPoint(sketch, "E122.visualSharp", {"position": v(-11.2, 26.25) * mm});
            skArc(sketch, "E122.filletArc", {"start": v(-10.5, 26.96) * mm, "mid": v(-10.79, 26.25) * mm, "end": v(-10.5, 25.54) * mm});
            skLineSegment(sketch, "E123.MirrorCS", {"start": v(11.2, 26.25) * mm, "end": v(4.2, 26.25) * mm});
            skLineSegment(sketch, "E124.MirrorCS", {"start": v(5.9, 31.54) * mm, "end": v(10.5, 26.96) * mm});
            skArc(sketch, "E125.MirrorCS", {"start": v(10.5, 26.96) * mm, "mid": v(10.79, 26.25) * mm, "end": v(10.5, 25.54) * mm});
            skLineSegment(sketch, "E126.MirrorCS", {"start": v(4.2, 26.25) * mm, "end": v(4.2, 30.84) * mm});
            skArc(sketch, "E127.MirrorCS", {"start": v(4.2, 30.84) * mm, "mid": v(4.82, 31.76) * mm, "end": v(5.9, 31.54) * mm});
            skPoint(sketch, "E128.MirrorP", {"position": v(4.2, 19.25) * mm});
            skArc(sketch, "E129.MirrorCS", {"start": v(5.9, 20.96) * mm, "mid": v(4.82, 20.74) * mm, "end": v(4.2, 21.66) * mm});
            skLineSegment(sketch, "E130.MirrorCS", {"start": v(5.9, 20.96) * mm, "end": v(10.5, 25.54) * mm});
            skLineSegment(sketch, "E131.MirrorCS", {"start": v(4.2, 26.25) * mm, "end": v(4.2, 21.66) * mm});
            skPoint(sketch, "E132.MirrorP", {"position": v(11.2, 26.25) * mm});
            skCircle(sketch, "E133", {"center": v(8.02, 37.45) * mm, "radius": 3.33 * mm});
            skCircle(sketch, "E134.MirrorC", {"center": v(-8.02, 37.45) * mm, "radius": 3.33 * mm});
            skCircle(sketch, "E135", {"center": v(8.63, 17.26) * mm, "radius": 1.72 * mm});
            skCircle(sketch, "E136.MirrorC", {"center": v(-8.63, 17.26) * mm, "radius": 1.72 * mm});
            skCircle(sketch, "E137", {"center": v(7.28, 70.44) * mm, "radius": 3.7 * mm});
            skLineSegment(sketch, "E138", {"start": v(0, 66.74) * mm, "end": v(7.28, 66.74) * mm});
            skCircle(sketch, "E139.MirrorC", {"center": v(-7.28, 70.44) * mm, "radius": 3.7 * mm});
            skLineSegment(sketch, "E140", {"start": v(9.9, 73.05) * mm, "end": v(7.98, 74.96) * mm});
            skLineSegment(sketch, "E141", {"start": v(6.57, 74.96) * mm, "end": v(4.66, 73.05) * mm});
            skPoint(sketch, "E142.visualSharp", {"position": v(7.28, 75.67) * mm});
            skArc(sketch, "E142.filletArc", {"start": v(7.98, 74.96) * mm, "mid": v(7.28, 75.25) * mm, "end": v(6.57, 74.96) * mm});
            skLineSegment(sketch, "E143.MirrorCS", {"start": v(-6.57, 74.96) * mm, "end": v(-4.66, 73.05) * mm});
            skLineSegment(sketch, "E144.MirrorCS", {"start": v(-9.9, 73.05) * mm, "end": v(-7.98, 74.96) * mm});
            skArc(sketch, "E145.MirrorCS", {"start": v(-7.98, 74.96) * mm, "mid": v(-7.28, 75.25) * mm, "end": v(-6.57, 74.96) * mm});
            skCircle(sketch, "E146", {"center": v(0, 34.28) * mm, "radius": 3.04 * mm});
            skLineSegment(sketch, "E147", {"start": v(-9.3, 57.76) * mm, "end": v(-5.77, 61.29) * mm});
            skLineSegment(sketch, "E148", {"start": v(-5.77, 62) * mm, "end": v(-8.44, 64.67) * mm});
            skLineSegment(sketch, "E149", {"start": v(-10.15, 63.97) * mm, "end": v(-10.15, 58.11) * mm});
            skPoint(sketch, "E150.visualSharp", {"position": v(-10.15, 56.9) * mm});
            skArc(sketch, "E150.filletArc", {"start": v(-10.15, 58.11) * mm, "mid": v(-9.84, 57.65) * mm, "end": v(-9.3, 57.76) * mm});
            skPoint(sketch, "E151.visualSharp", {"position": v(-5.41, 61.64) * mm});
            skArc(sketch, "E151.filletArc", {"start": v(-5.77, 61.29) * mm, "mid": v(-5.62, 61.64) * mm, "end": v(-5.77, 62) * mm});
            skPoint(sketch, "E152.visualSharp", {"position": v(-10.15, 66.38) * mm});
            skArc(sketch, "E152.filletArc", {"start": v(-8.44, 64.67) * mm, "mid": v(-9.53, 64.89) * mm, "end": v(-10.15, 63.97) * mm});
            skCircle(sketch, "E153", {"center": v(-4.2, 65.01) * mm, "radius": 1.53 * mm});
            skCircle(sketch, "E154.MirrorC", {"center": v(4.2, 65.01) * mm, "radius": 1.53 * mm});
            skArc(sketch, "E155.MirrorCS", {"start": v(10.15, 58.11) * mm, "mid": v(9.84, 57.65) * mm, "end": v(9.3, 57.76) * mm});
            skArc(sketch, "E156.MirrorCS", {"start": v(5.77, 61.29) * mm, "mid": v(5.62, 61.64) * mm, "end": v(5.77, 62) * mm});
            skPoint(sketch, "E157.MirrorP", {"position": v(10.15, 56.9) * mm});
            skLineSegment(sketch, "E158.MirrorCS", {"start": v(9.3, 57.76) * mm, "end": v(5.77, 61.29) * mm});
            skLineSegment(sketch, "E159.MirrorCS", {"start": v(10.15, 63.97) * mm, "end": v(10.15, 58.11) * mm});
            skPoint(sketch, "E160.MirrorP", {"position": v(5.41, 61.64) * mm});
            skArc(sketch, "E161.MirrorCS", {"start": v(8.44, 64.67) * mm, "mid": v(9.53, 64.89) * mm, "end": v(10.15, 63.97) * mm});
            skLineSegment(sketch, "E162.MirrorCS", {"start": v(5.77, 62) * mm, "end": v(8.44, 64.67) * mm});
            skSolve(sketch);
        }
        {
            var Q0;
            Q0=qSketchRegion(id+"F22",true);
            var Q1;
            {var subQ0=sQuery(id+"F1.wireOp",EDGE,"E37.MirrorCS");var subQ1=makeQuery(id+"F2.opExtrude","SWEPT_FACE",FACE,{"disambiguationData":[OSD([subQ0])]});var subQ2=sQuery(id+"F1.wireOp",EDGE,"E36.MirrorCS");var subQ3=sQuery(id+"F1.wireOp",EDGE,"E35");var subQ4=sQuery(id+"F1.wireOp",EDGE,"E38.MirrorCS");Q1=makeQuery(id+"F8.boolean.opBoolean","SPLIT",FACE,{"disambiguationData":[TD([makeQuery(id+"F2.opExtrude","CAP_FACE",FACE,{"disambiguationData":[OSD([sQuery(id+"F1.wireOp",EDGE,"E24"),sQuery(id+"F1.wireOp",EDGE,"E25"),sQuery(id+"F1.wireOp",EDGE,"E31"),sQuery(id+"F1.wireOp",EDGE,"E32"),sQuery(id+"F1.wireOp",EDGE,"E33"),sQuery(id+"F1.wireOp",EDGE,"E34"),subQ3,subQ2,subQ0,subQ4])],"isStart":true})])],"derivedFrom":subQ1});}
            extrude(context, id + "F23", {"entities" : qUnion([Q0]), "operationType" : NewBodyOperationType.REMOVE, "endBound" : BoundingType.UP_TO_SURFACE, "endBoundEntityFace" : qUnion([Q1]), "depth" : 8 * mm});
        }
        {
            var Q0;
            Q0=makeQuery(id+"F8.boolean.opBoolean","MERGE",FACE,{"derivedFrom":[makeQuery(id+"F2.opExtrude","SWEPT_FACE",FACE,{"disambiguationData":[OSD([sQuery(id+"F1.wireOp",EDGE,"E24"),sQuery(id+"F1.wireOp",EDGE,"E25")])]}),makeQuery(id+"F8.opExtrude","CAP_FACE",FACE,{"disambiguationData":[OSD([sQuery(id+"F7.wireOp",EDGE,"E41"),sQuery(id+"F7.wireOp",EDGE,"E42"),sQuery(id+"F7.wireOp",EDGE,"E44"),sQuery(id+"F7.wireOp",EDGE,"E45.MirrorCS"),sQuery(id+"F7.wireOp",EDGE,"E46.MirrorCS"),sQuery(id+"F7.wireOp",EDGE,"E47.MirrorCS"),sQuery(id+"F7.wireOp",EDGE,"E48.trimOffspring")])],"isStart":true})]});
            var sketch = newSketch(context, id + "F24", { "sketchPlane" : qUnion([Q0])});
            skLineSegment(sketch, "E163", {"start": v(11.35, -16.5) * mm, "end": v(11.35, -9.42) * mm});
            skLineSegment(sketch, "E164.MirrorCS", {"start": v(-11.35, -16.5) * mm, "end": v(-11.35, -9.42) * mm});
            skLineSegment(sketch, "E165", {"start": v(11.35, -16.5) * mm, "end": v(11.35, -12.6) * mm});
            skLineSegment(sketch, "E166", {"start": v(15.25, -4.5) * mm, "end": v(15.25, -12.6) * mm});
            skLineSegment(sketch, "E167.MirrorCS", {"start": v(-15.25, -4.5) * mm, "end": v(-15.25, -12.6) * mm});
            skLineSegment(sketch, "E168", {"start": v(11.35, -12.6) * mm, "end": v(11.35, -9.42) * mm});
            skLineSegment(sketch, "E169", {"start": v(11.35, -16.5) * mm, "end": v(15.25, -12.6) * mm});
            skLineSegment(sketch, "E170", {"start": v(-11.35, -16.5) * mm, "end": v(-15.25, -12.6) * mm});
            skLineSegment(sketch, "E171", {"start": v(11.35, -10.22) * mm, "end": v(15.25, -4.5) * mm});
            skLineSegment(sketch, "E172.MirrorCS", {"start": v(-11.35, -10.22) * mm, "end": v(-15.25, -4.5) * mm});
            skPoint(sketch, "E173.MirrorCS.end.orphan", {"position": v(-15.25, -4.5) * mm});
            skSolve(sketch);
        }
        {
            var Q0;
            Q0 = qSketchRegion(id + "F24", true);
            var Q1;
            {var subQ0=sQuery(id+"F1.wireOp",EDGE,"E38.MirrorCS");var subQ1=sQuery(id+"F1.wireOp",EDGE,"E37.MirrorCS");var subQ2=sQuery(id+"F1.wireOp",EDGE,"E36.MirrorCS");var subQ3=sQuery(id+"F1.wireOp",EDGE,"E35");var subQ4=sQuery(id+"F1.wireOp",EDGE,"E34");var subQ5=sQuery(id+"F1.wireOp",EDGE,"E33");var subQ6=sQuery(id+"F1.wireOp",EDGE,"E32");var subQ7=sQuery(id+"F1.wireOp",EDGE,"E31");var subQ8=sQuery(id+"F1.wireOp",EDGE,"E25");var subQ9=sQuery(id+"F1.wireOp",EDGE,"E24");var subQ13=makeQuery(id+"F2.opExtrude","SWEPT_FACE",FACE,{"disambiguationData":[OSD([subQ3,subQ2])]});Q1=makeQuery(id+"F8.boolean.opBoolean","MERGE",FACE,{"derivedFrom":[makeQuery(id+"F5.boolean.opBoolean","SPLIT",FACE,{"disambiguationData":[TD([makeQuery(id+"F2.opExtrude","CAP_FACE",FACE,{"disambiguationData":[OSD([subQ9,subQ8,subQ7,subQ6,subQ5,subQ4,subQ3,subQ2,subQ1,subQ0])],"isStart":true})])],"derivedFrom":subQ13}),makeQuery(id+"F5.boolean.opBoolean","SPLIT",FACE,{"disambiguationData":[TD([makeQuery(id+"F2.opExtrude","CAP_FACE",FACE,{"disambiguationData":[OSD([subQ9,subQ8,subQ7,subQ6,subQ5,subQ4,subQ3,subQ2,subQ1,subQ0])],"isStart":false})])],"derivedFrom":subQ13}),makeQuery(id+"F8.opExtrude","CAP_FACE",FACE,{"disambiguationData":[OSD([sQuery(id+"F7.wireOp",EDGE,"E41"),sQuery(id+"F7.wireOp",EDGE,"E42"),sQuery(id+"F7.wireOp",EDGE,"E44"),sQuery(id+"F7.wireOp",EDGE,"E45.MirrorCS"),sQuery(id+"F7.wireOp",EDGE,"E46.MirrorCS"),sQuery(id+"F7.wireOp",EDGE,"E47.MirrorCS"),sQuery(id+"F7.wireOp",EDGE,"E48.trimOffspring")])],"isStart":false})]});}
            extrude(context, id + "F25", {"entities" : qUnion([Q0]), "operationType" : NewBodyOperationType.ADD, "endBound" : BoundingType.UP_TO_SURFACE, "oppositeDirection" : true, "endBoundEntityFace" : qUnion([Q1]), "depth" : 25 * mm});
        }
        {
            var Q0;
            Q0=makeQuery(id+"F5.boolean.opBoolean","COPY",EDGE,{"derivedFrom":makeQuery(id+"F5.opExtrude","CAP_EDGE",EDGE,{"disambiguationData":[OSD([sQuery(id+"F4.wireOp",EDGE,"E39")])],"isStart":false})});
            fillet(context, id + "F26", {"entities" : qUnion([Q0]), "radius" : 1.5 * mm, "tangentPropagation" : true, "allowEdgeOverflow" : false});
        }
        {
            var Q0;
            Q0=makeQuery(id+"F12.boolean.opBoolean","COPY",EDGE,{"derivedFrom":makeQuery(id+"F12.opExtrude","CAP_EDGE",EDGE,{"disambiguationData":[OSD([sQuery(id+"F11.wireOp",EDGE,"E59.MirrorC")])],"isStart":false})});
            var Q1;
            Q1=makeQuery(id+"F12.boolean.opBoolean","COPY",EDGE,{"derivedFrom":makeQuery(id+"F12.opExtrude","CAP_EDGE",EDGE,{"disambiguationData":[OSD([sQuery(id+"F11.wireOp",EDGE,"E54")])],"isStart":false})});
            var Q2;
            Q2=makeQuery(id+"F12.boolean.opBoolean","COPY",EDGE,{"derivedFrom":makeQuery(id+"F12.opExtrude","CAP_EDGE",EDGE,{"disambiguationData":[OSD([sQuery(id+"F11.wireOp",EDGE,"E58")])],"isStart":false})});
            var Q3;
            Q3=makeQuery(id+"F12.boolean.opBoolean","COPY",EDGE,{"derivedFrom":makeQuery(id+"F12.opExtrude","CAP_EDGE",EDGE,{"disambiguationData":[OSD([sQuery(id+"F11.wireOp",EDGE,"E56")])],"isStart":false})});
            fillet(context, id + "F27", {"entities" : qUnion([Q0, Q1, Q2, Q3]), "radius" : .4 * mm, "tangentPropagation" : true, "allowEdgeOverflow" : false});
        }
    });
